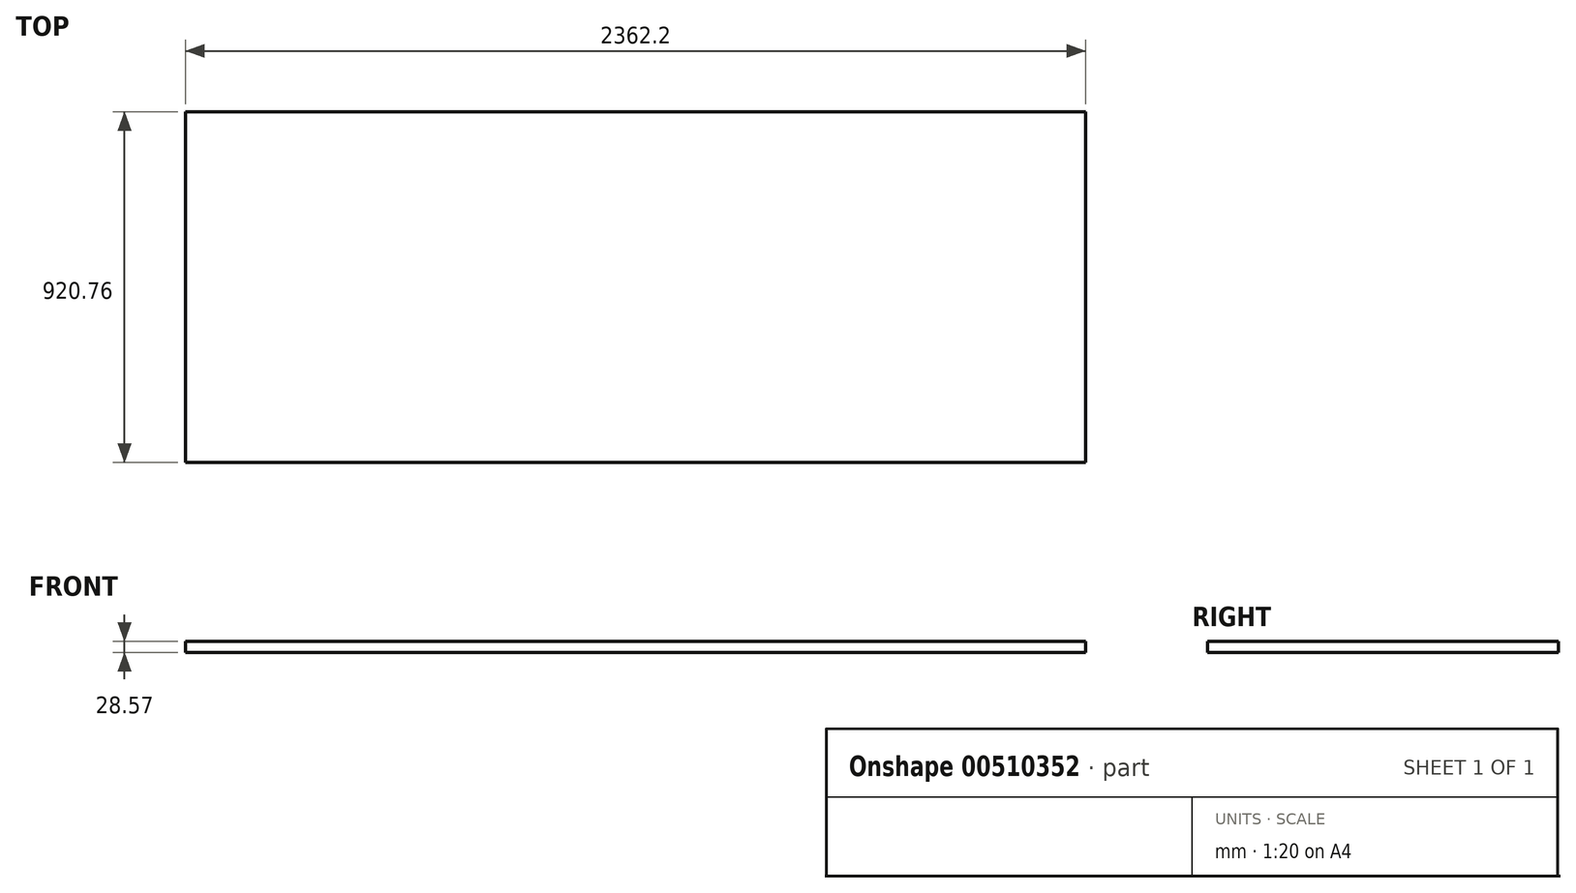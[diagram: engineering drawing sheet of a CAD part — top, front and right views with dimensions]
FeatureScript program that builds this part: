
annotation { "Feature Type Name" : "Feature", "Feature Type Description" : "" }
export const myFeature = defineFeature(function(context is Context, id is Id, definition is map)
    precondition{}
    {
        {
            var Q0;
            Q0=qCreatedBy(makeId("Top.planeOp"),FACE);
            var sketch = newSketch(context, id + "F0", { "sketchPlane" : qUnion([Q0])});
            skLineSegment(sketch, "E0.bottom", {"start": v(-1181.1, 460.38) * mm, "end": v(1181.1, 460.38) * mm});
            skLineSegment(sketch, "E0.top", {"start": v(-1181.1, -460.38) * mm, "end": v(1181.1, -460.38) * mm});
            skLineSegment(sketch, "E0.left", {"start": v(-1181.1, 460.38) * mm, "end": v(-1181.1, -460.38) * mm});
            skLineSegment(sketch, "E0.right", {"start": v(1181.1, 460.38) * mm, "end": v(1181.1, -460.38) * mm});
            skPoint(sketch, "E0.middle", {"position": v(0, 0) * mm});
            skSolve(sketch);
        }
        {
            var Q0;
            Q0 = qSketchRegion(id + "F0", true);
            extrude(context, id + "F1", {"entities" : qUnion([Q0]), "depth" : 28.57 * mm});
        }
    });
